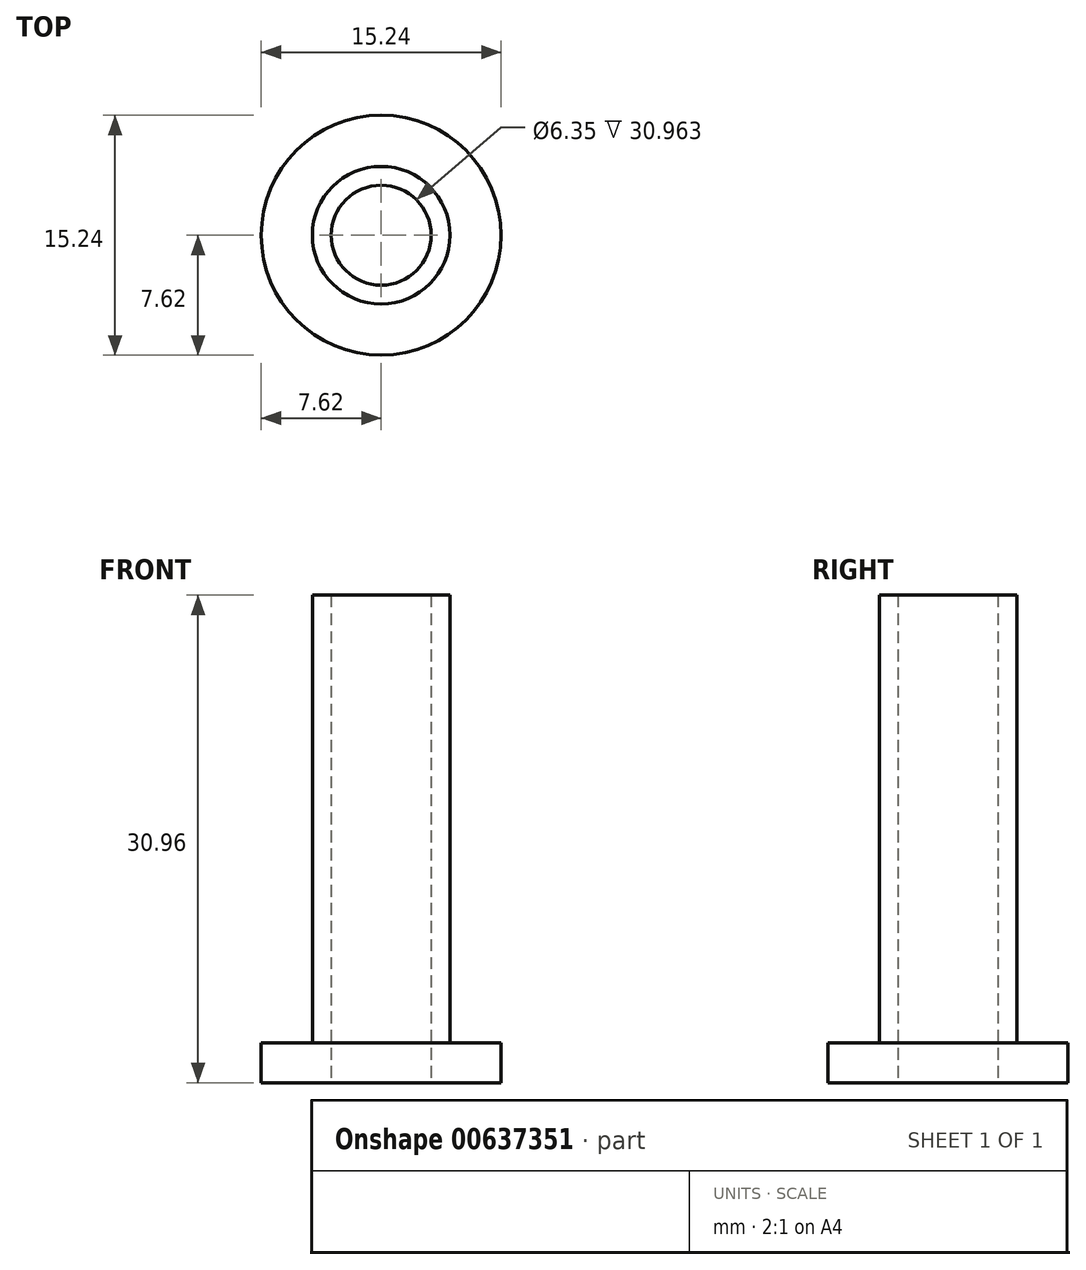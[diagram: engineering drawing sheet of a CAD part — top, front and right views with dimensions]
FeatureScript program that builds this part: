
annotation { "Feature Type Name" : "Feature", "Feature Type Description" : "" }
export const myFeature = defineFeature(function(context is Context, id is Id, definition is map)
    precondition{}
    {
        {
            var Q0;
            Q0=qCreatedBy(makeId("Top.planeOp"),FACE);
            var sketch = newSketch(context, id + "F0", { "sketchPlane" : qUnion([Q0])});
            skCircle(sketch, "E0", {"center": v(0, 0) * mm, "radius": 4.37 * mm});
            skCircle(sketch, "E1", {"center": v(0, 0) * mm, "radius": 7.62 * mm});
            skCircle(sketch, "E2", {"center": v(0, 0) * mm, "radius": 3.17 * mm});
            skSolve(sketch);
        }
        {
            var Q0;
            Q0=makeQuery(id+"F0.imprint","IMPRINT",FACE,{"disambiguationData":[TD([[makeQuery(id+"F0.imprint","IMPRINT",EDGE,{"derivedFrom":sQuery(id+"F0.wireOp",EDGE,"E0")}),1.0]])]});
            extrude(context, id + "F1", {"entities" : qUnion([Q0]), "depth" : 28.42 * mm, "offsetDistance" : 25.4 * mm, "hasSecondDirection" : true, "secondDirectionOppositeDirection" : true, "secondDirectionDepth" : 2.54 * mm});
        }
        {
            var Q0;
            Q0=makeQuery(id+"F0.imprint","IMPRINT",FACE,{"disambiguationData":[TD([[makeQuery(id+"F0.imprint","IMPRINT",EDGE,{"derivedFrom":sQuery(id+"F0.wireOp",EDGE,"E0")}),-1.0]])]});
            extrude(context, id + "F2", {"entities" : qUnion([Q0]), "operationType" : NewBodyOperationType.ADD, "oppositeDirection" : true, "depth" : 2.54 * mm, "offsetDistance" : 25.4 * mm});
        }
    });
